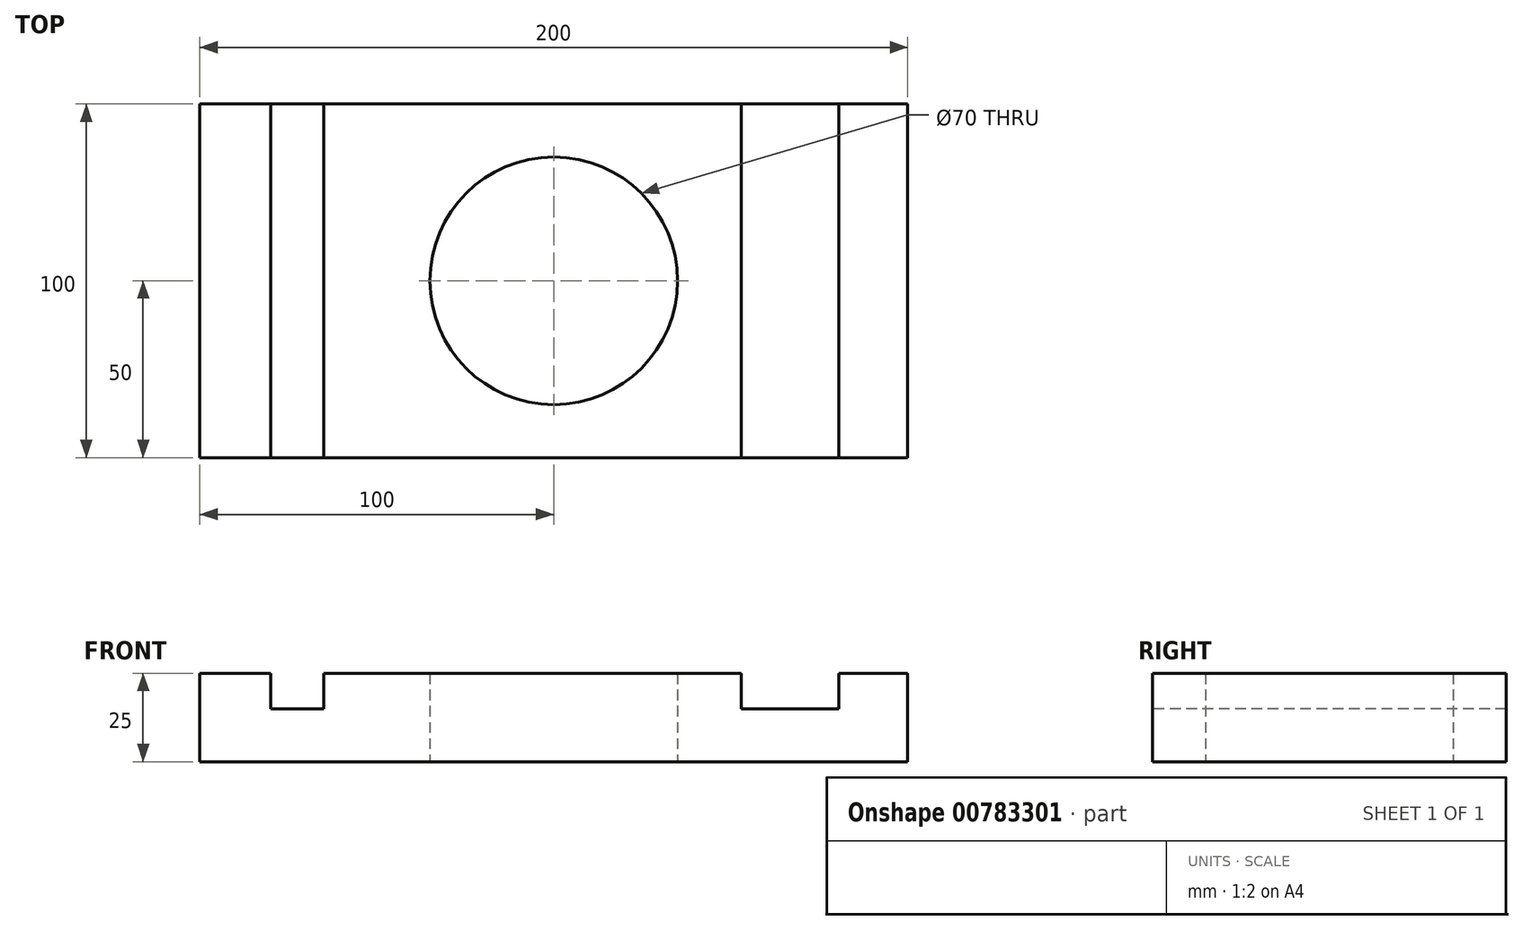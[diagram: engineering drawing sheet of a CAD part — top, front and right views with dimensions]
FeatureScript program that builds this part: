
annotation { "Feature Type Name" : "Feature", "Feature Type Description" : "" }
export const myFeature = defineFeature(function(context is Context, id is Id, definition is map)
    precondition{}
    {
        {
            var Q0;
            Q0=qCreatedBy(makeId("Top.planeOp"),FACE);
            var sketch = newSketch(context, id + "F0", { "sketchPlane" : qUnion([Q0])});
            skLineSegment(sketch, "E0.bottom", {"start": v(100, 50) * mm, "end": v(-100, 50) * mm});
            skLineSegment(sketch, "E0.top", {"start": v(100, -50) * mm, "end": v(-100, -50) * mm});
            skLineSegment(sketch, "E0.left", {"start": v(100, 50) * mm, "end": v(100, -50) * mm});
            skLineSegment(sketch, "E0.right", {"start": v(-100, 50) * mm, "end": v(-100, -50) * mm});
            skPoint(sketch, "E0.middle", {"position": v(0, 0) * mm});
            skCircle(sketch, "E1", {"center": v(0, 0) * mm, "radius": 35 * mm});
            skSolve(sketch);
        }
        {
            var Q0;
            Q0=makeQuery(id+"F0.imprint","IMPRINT",FACE,{"disambiguationData":[TD([[makeQuery(id+"F0.imprint","IMPRINT",EDGE,{"derivedFrom":sQuery(id+"F0.wireOp",EDGE,"E0.bottom")}),1.0]])]});
            extrude(context, id + "F1", {"entities" : qUnion([Q0]), "depth" : 25 * mm, "offsetDistance" : 25 * mm});
        }
        {
            var Q0;
            Q0=makeQuery(id+"F1.opExtrude","CAP_FACE",FACE,{"disambiguationData":[OSD([sQuery(id+"F0.wireOp",EDGE,"E0.bottom"),sQuery(id+"F0.wireOp",EDGE,"E0.top"),sQuery(id+"F0.wireOp",EDGE,"E0.left"),sQuery(id+"F0.wireOp",EDGE,"E0.right"),sQuery(id+"F0.wireOp",EDGE,"E1")])],"isStart":false});
            var sketch = newSketch(context, id + "F2", { "sketchPlane" : qUnion([Q0])});
            skLineSegment(sketch, "E2.bottom", {"start": v(-80, 50) * mm, "end": v(-65, 50) * mm});
            skLineSegment(sketch, "E2.top", {"start": v(-80, -50) * mm, "end": v(-65, -50) * mm});
            skLineSegment(sketch, "E2.left", {"start": v(-80, 50) * mm, "end": v(-80, -50) * mm});
            skLineSegment(sketch, "E2.right", {"start": v(-65, 50) * mm, "end": v(-65, -50) * mm});
            skSolve(sketch);
        }
        {
            var Q0;
            Q0 = qSketchRegion(id + "F2", true);
            extrude(context, id + "F3", {"entities" : qUnion([Q0]), "operationType" : NewBodyOperationType.REMOVE, "oppositeDirection" : true, "depth" : 10 * mm, "offsetDistance" : 25 * mm});
        }
        {
            var Q0;
            {var subQ0=sQuery(id+"F0.wireOp",EDGE,"E1");var subQ1=sQuery(id+"F0.wireOp",EDGE,"E0.left");var subQ2=sQuery(id+"F0.wireOp",EDGE,"E0.top");var subQ3=sQuery(id+"F0.wireOp",EDGE,"E0.bottom");Q0=makeQuery(id+"F3.boolean.opBoolean","SPLIT",FACE,{"disambiguationData":[TD([makeQuery(id+"F1.opExtrude","SWEPT_FACE",FACE,{"disambiguationData":[OSD([subQ1])]})])],"derivedFrom":makeQuery(id+"F1.opExtrude","CAP_FACE",FACE,{"disambiguationData":[OSD([subQ3,subQ2,subQ1,sQuery(id+"F0.wireOp",EDGE,"E0.right"),subQ0])],"isStart":false})});}
            var sketch = newSketch(context, id + "F4", { "sketchPlane" : qUnion([Q0])});
            skLineSegment(sketch, "E3.bottom", {"start": v(52.98, 50) * mm, "end": v(80.58, 50) * mm});
            skLineSegment(sketch, "E3.top", {"start": v(52.98, -50) * mm, "end": v(80.58, -50) * mm});
            skLineSegment(sketch, "E3.left", {"start": v(52.98, 50) * mm, "end": v(52.98, -50) * mm});
            skLineSegment(sketch, "E3.right", {"start": v(80.58, 50) * mm, "end": v(80.58, -50) * mm});
            skSolve(sketch);
        }
        {
            var Q0;
            Q0 = qSketchRegion(id + "F4", true);
            extrude(context, id + "F5", {"entities" : qUnion([Q0]), "operationType" : NewBodyOperationType.REMOVE, "oppositeDirection" : true, "depth" : 10 * mm, "offsetDistance" : 25 * mm});
        }
    });
